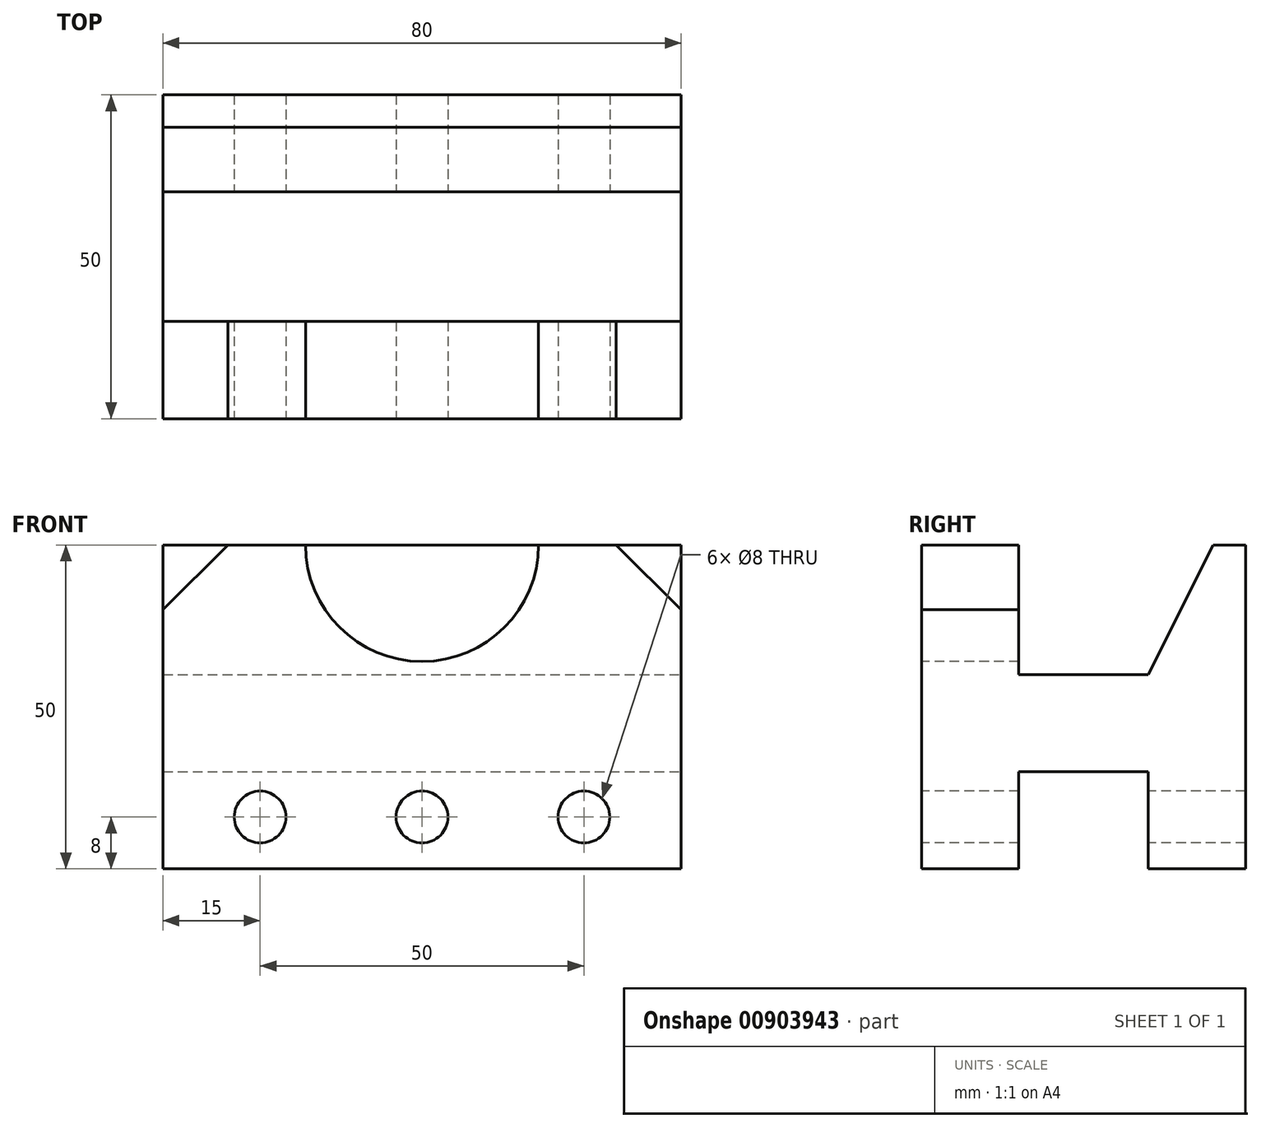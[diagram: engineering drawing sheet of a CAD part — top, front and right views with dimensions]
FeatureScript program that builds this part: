
annotation { "Feature Type Name" : "Feature", "Feature Type Description" : "" }
export const myFeature = defineFeature(function(context is Context, id is Id, definition is map)
    precondition{}
    {
        {
            var Q0;
            Q0=qCreatedBy(makeId("Top.planeOp"),FACE);
            var sketch = newSketch(context, id + "F0", { "sketchPlane" : qUnion([Q0])});
            skLineSegment(sketch, "E0.bottom", {"start": v(40, -25) * mm, "end": v(-40, -25) * mm});
            skLineSegment(sketch, "E0.top", {"start": v(40, 25) * mm, "end": v(-40, 25) * mm});
            skLineSegment(sketch, "E0.left", {"start": v(40, -25) * mm, "end": v(40, 25) * mm});
            skLineSegment(sketch, "E0.right", {"start": v(-40, -25) * mm, "end": v(-40, 25) * mm});
            skPoint(sketch, "E0.middle", {"position": v(0, 0) * mm});
            skSolve(sketch);
        }
        {
            var Q0;
            Q0=makeQuery(id+"F0.imprint","IMPRINT",FACE,{"disambiguationData":[TD([[makeQuery(id+"F0.imprint","IMPRINT",EDGE,{"derivedFrom":sQuery(id+"F0.wireOp",EDGE,"E0.bottom")}),-1.0]])]});
            extrude(context, id + "F1", {"entities" : qUnion([Q0]), "depth" : 50 * mm, "offsetDistance" : 25 * mm});
        }
        {
            var Q0;
            Q0=makeQuery(id+"F1.opExtrude","SWEPT_FACE",FACE,{"disambiguationData":[OSD([sQuery(id+"F0.wireOp",EDGE,"E0.left")])]});
            var sketch = newSketch(context, id + "F2", { "sketchPlane" : qUnion([Q0])});
            skLineSegment(sketch, "E1.bottom", {"start": v(-10, 15) * mm, "end": v(10, 15) * mm});
            skLineSegment(sketch, "E1.top", {"start": v(-10, 0) * mm, "end": v(10, 0) * mm});
            skLineSegment(sketch, "E1.left", {"start": v(-10, 15) * mm, "end": v(-10, 0) * mm});
            skLineSegment(sketch, "E1.right", {"start": v(10, 15) * mm, "end": v(10, 0) * mm});
            skSolve(sketch);
        }
        {
            var Q0;
            Q0=makeQuery(id+"F2.imprint","IMPRINT",FACE,{"disambiguationData":[TD([[makeQuery(id+"F2.imprint","IMPRINT",EDGE,{"derivedFrom":sQuery(id+"F2.wireOp",EDGE,"E1.bottom")}),-1.0]])]});
            extrude(context, id + "F3", {"entities" : qUnion([Q0]), "operationType" : NewBodyOperationType.REMOVE, "endBound" : BoundingType.THROUGH_ALL, "oppositeDirection" : true, "depth" : 25 * mm, "offsetDistance" : 25 * mm});
        }
        {
            var Q0;
            Q0=makeQuery(id+"F1.opExtrude","SWEPT_FACE",FACE,{"disambiguationData":[OSD([sQuery(id+"F0.wireOp",EDGE,"E0.left")])]});
            var sketch = newSketch(context, id + "F4", { "sketchPlane" : qUnion([Q0])});
            skLineSegment(sketch, "E2", {"start": v(-10, 50) * mm, "end": v(-10, 30) * mm});
            skLineSegment(sketch, "E3", {"start": v(-10, 30) * mm, "end": v(10, 30) * mm});
            skLineSegment(sketch, "E4", {"start": v(10, 30) * mm, "end": v(20, 50) * mm});
            skSolve(sketch);
        }
        {
            var Q0;
            {var subQ0=sQuery(id+"F4.wireOp",EDGE,"E2");Q0=makeQuery(id+"F4.imprint","IMPRINT",FACE,{"disambiguationData":[TD([[makeQuery(id+"F4.imprint","IMPRINT",EDGE,{"derivedFrom":subQ0}),1.0]])]});}
            extrude(context, id + "F5", {"entities" : qUnion([Q0]), "operationType" : NewBodyOperationType.REMOVE, "endBound" : BoundingType.THROUGH_ALL, "oppositeDirection" : true, "depth" : 25 * mm, "offsetDistance" : 25 * mm});
        }
        {
            var Q0;
            Q0=makeQuery(id+"F1.opExtrude","SWEPT_FACE",FACE,{"disambiguationData":[OSD([sQuery(id+"F0.wireOp",EDGE,"E0.bottom")])]});
            var sketch = newSketch(context, id + "F6", { "sketchPlane" : qUnion([Q0])});
            skCircle(sketch, "E5", {"center": v(0, 50) * mm, "radius": 18 * mm});
            skSolve(sketch);
        }
        {
            var Q0;
            {var subQ0=sQuery(id+"F6.wireOp",EDGE,"E5");var subQ1=makeQuery(id+"F1.opExtrude","CAP_EDGE",EDGE,{"disambiguationData":[OSD([sQuery(id+"F0.wireOp",EDGE,"E0.bottom")])],"isStart":false});var subQ2=makeQuery(id+"F6.imprint","INTERSECT",VERTEX,{"disambiguationData":[OD(0.0)],"derivedFrom":[subQ1,subQ0]});Q0=makeQuery(id+"F6.imprint","IMPRINT",FACE,{"disambiguationData":[TD([[makeQuery(id+"F6.imprint","IMPRINT",EDGE,{"disambiguationData":[TD([[subQ2,1.0]])],"derivedFrom":subQ0}),1.0]])]});}
            extrude(context, id + "F7", {"entities" : qUnion([Q0]), "operationType" : NewBodyOperationType.REMOVE, "endBound" : BoundingType.UP_TO_NEXT, "oppositeDirection" : true, "depth" : 25 * mm, "offsetDistance" : 25 * mm});
        }
        {
            var Q0;
            {var subQ0=sQuery(id+"F0.wireOp",EDGE,"E0.bottom");var subQ1=sQuery(id+"F0.wireOp",EDGE,"E0.left");Q0=makeQuery(id+"F5.boolean.opBoolean","SPLIT",EDGE,{"disambiguationData":[TD([makeQuery(id+"F1.opExtrude","SWEPT_FACE",FACE,{"disambiguationData":[OSD([subQ0])]})])],"derivedFrom":makeQuery(id+"F1.opExtrude","CAP_EDGE",EDGE,{"disambiguationData":[OSD([subQ1])],"isStart":false})});}
            var Q1;
            {var subQ0=sQuery(id+"F0.wireOp",EDGE,"E0.bottom");var subQ1=sQuery(id+"F0.wireOp",EDGE,"E0.right");Q1=makeQuery(id+"F5.boolean.opBoolean","SPLIT",EDGE,{"disambiguationData":[TD([makeQuery(id+"F1.opExtrude","SWEPT_FACE",FACE,{"disambiguationData":[OSD([subQ0])]})])],"derivedFrom":makeQuery(id+"F1.opExtrude","CAP_EDGE",EDGE,{"disambiguationData":[OSD([subQ1])],"isStart":false})});}
            chamfer(context, id + "F8", {"entities" : qUnion([Q0, Q1]), "width" : 10 * mm, "tangentPropagation" : true});
        }
        {
            var Q0;
            Q0=makeQuery(id+"F1.opExtrude","SWEPT_FACE",FACE,{"disambiguationData":[OSD([sQuery(id+"F0.wireOp",EDGE,"E0.bottom")])]});
            var sketch = newSketch(context, id + "F9", { "sketchPlane" : qUnion([Q0])});
            skLineSegment(sketch, "E6.0", {"start": v(40, 8) * mm, "end": v(-40, 8) * mm, "construction": true});
            skCircle(sketch, "E7", {"center": v(0, 8) * mm, "radius": 4 * mm});
            skLineSegment(sketch, "E8.0", {"start": v(0, 57.15) * mm, "end": v(0, -8.5) * mm, "construction": true});
            skLineSegment(sketch, "E9.0", {"start": v(-25, 57.15) * mm, "end": v(-25, -8.5) * mm, "construction": true});
            skLineSegment(sketch, "E10.MirrorCS", {"start": v(25, 57.15) * mm, "end": v(25, -8.5) * mm, "construction": true});
            skCircle(sketch, "E11", {"center": v(-25, 8) * mm, "radius": 4 * mm});
            skCircle(sketch, "E12", {"center": v(25, 8) * mm, "radius": 4 * mm});
            skSolve(sketch);
        }
        {
            var Q0;
            Q0=makeQuery(id+"F9.imprint","IMPRINT",FACE,{"disambiguationData":[TD([[makeQuery(id+"F9.imprint","IMPRINT",EDGE,{"derivedFrom":sQuery(id+"F9.wireOp",EDGE,"E11")}),1.0]])]});
            var Q1;
            Q1=makeQuery(id+"F9.imprint","IMPRINT",FACE,{"disambiguationData":[TD([[makeQuery(id+"F9.imprint","IMPRINT",EDGE,{"derivedFrom":sQuery(id+"F9.wireOp",EDGE,"E7")}),1.0]])]});
            var Q2;
            Q2=makeQuery(id+"F9.imprint","IMPRINT",FACE,{"disambiguationData":[TD([[makeQuery(id+"F9.imprint","IMPRINT",EDGE,{"derivedFrom":sQuery(id+"F9.wireOp",EDGE,"E12")}),1.0]])]});
            extrude(context, id + "F10", {"entities" : qUnion([Q0, Q1, Q2]), "operationType" : NewBodyOperationType.REMOVE, "endBound" : BoundingType.THROUGH_ALL, "oppositeDirection" : true, "depth" : 25 * mm, "offsetDistance" : 25 * mm});
        }
    });
